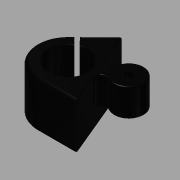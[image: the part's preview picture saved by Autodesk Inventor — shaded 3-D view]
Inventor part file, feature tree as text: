
AUTODESK INVENTOR PART (.ipt)
format: ipt  version: 2014 (Build 180170000, 170)  size: 419,840 bytes
history: native  units: mm
features: extrude x6, fillet x6, sketch x6, projected_geometry x5, plane x1
ambient origin geometry x8: Origin, YZ Plane, XZ Plane, XY Plane, X Axis, Y Axis, Z Axis, Center Point
bodies: Body1 (feature_tree)
feature tree (24):
  extrude  "Extrusion2"  Depth=226.0mm
  extrude  "Extrusion5"  Depth=26.0mm
  fillet  "Fillet1"  Radius=26.0mm
  extrude  "Extrusion7"  Depth=20.0mm
  extrude  "Extrusion8"  Depth=25.0mm
  extrude  "Extrusion9"  Depth=25.0mm
  fillet  "Fillet4"  Radius=25.0mm
  fillet  "Fillet5"  Radius=25.0mm
  plane  "Work Plane4"
  extrude  "Extrusion11"  Depth=1.0mm TaperAngle=0.0deg
  fillet  "Fillet7"  Radius=30.0mm
  fillet  "Fillet8"  Radius=19.0mm
  fillet  "Fillet11"  Radius=5.0mm
  sketch  "Sketch1"  dims[d0=113.0mm d1=226.0mm]
  sketch  "Sketch2"  dims[d2=110.0mm d3=26.0mm d5=26.0mm]
  projected_geometry  "Projected Loop1"
  sketch  "Sketch5"  dims[d14=20.0mm d17=20.0mm]
  projected_geometry  "Projected Loop4"
  sketch  "Sketch6"  dims[d18=20.0mm d19=25.0mm]
  projected_geometry  "Projected Loop5"
  sketch  "Sketch7"  dims[d20=20.0mm d21=25.0mm d22=25.0mm d23=25.0mm]
  projected_geometry  "Projected Loop6"
  sketch  "Sketch10"  dims[d24=22.0mm d27=30.0mm d28=0.0mm d33=30.0mm d34=19.0mm d35=5.0mm d41=5.0mm d42=5.0mm d43=18.0mm d44=0.0mm d45=3.0mm d58=2.3mm d59=5.3mm d60=20.0mm d61=0.0mm d62=5.0mm d63=3.5mm d64=60.0mm d65=0.0mm d66=7.5mm d67=2.5mm d68=15.0mm d69=0.0mm d71=5.0mm d72=0.0mm d79=2.0mm d80=0.5mm d82=-11.0mm d83=7.7mm d84=10.0mm d85=0.0mm d86=2.0mm d87=1.0mm d98=25.4mm d99=1.0mm]
  projected_geometry  "Projected Loop7"
